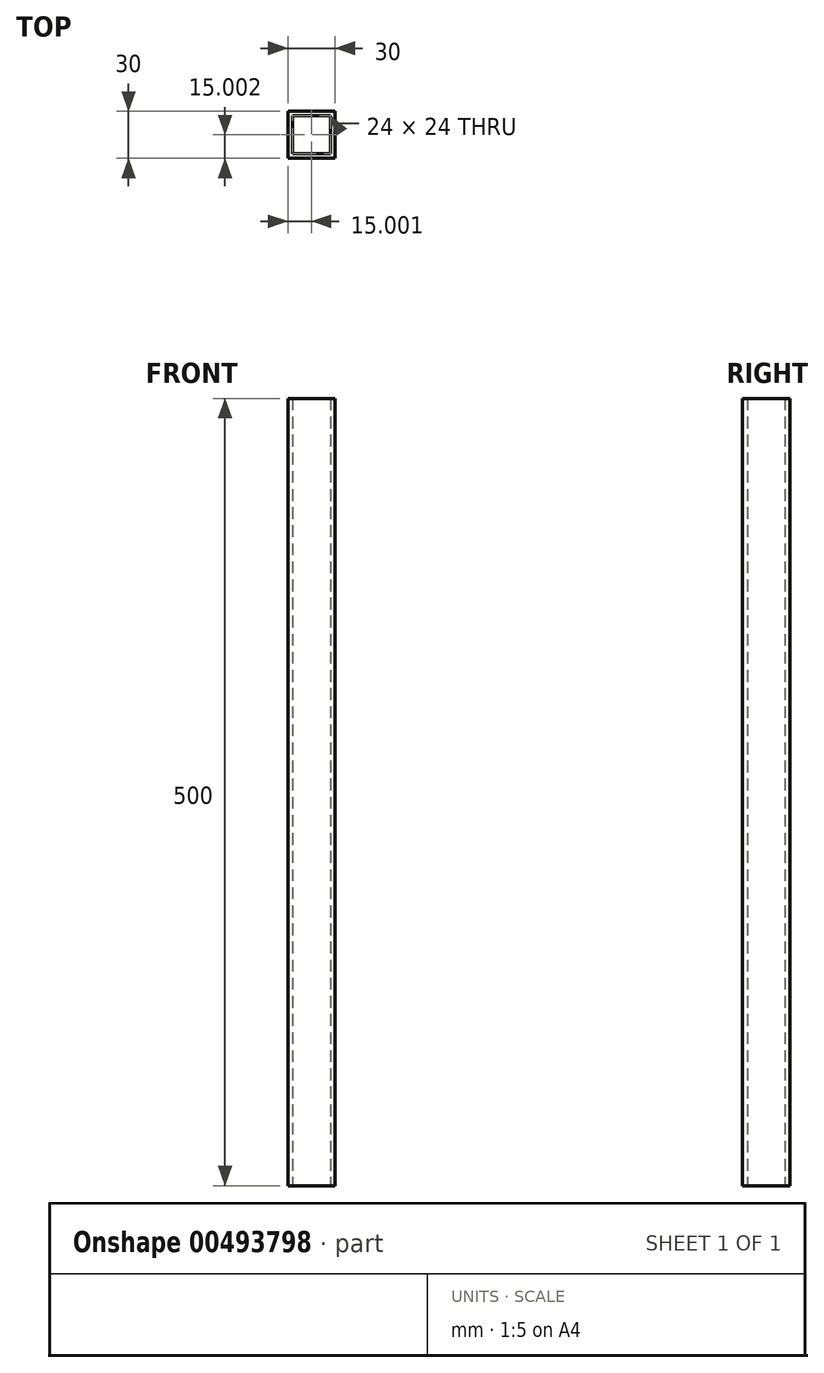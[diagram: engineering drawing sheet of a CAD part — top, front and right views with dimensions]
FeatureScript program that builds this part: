
annotation { "Feature Type Name" : "Feature", "Feature Type Description" : "" }
export const myFeature = defineFeature(function(context is Context, id is Id, definition is map)
    precondition{}
    {
        {
            var Q0;
            Q0=qCreatedBy(makeId("Top.planeOp"),FACE);
            var sketch = newSketch(context, id + "F0", { "sketchPlane" : qUnion([Q0])});
            skLineSegment(sketch, "E0.bottom", {"start": v(-12.6, 13.15) * mm, "end": v(11.4, 13.15) * mm});
            skLineSegment(sketch, "E0.top", {"start": v(-12.6, -10.85) * mm, "end": v(11.4, -10.85) * mm});
            skLineSegment(sketch, "E0.left", {"start": v(-12.6, 13.15) * mm, "end": v(-12.6, -10.85) * mm});
            skLineSegment(sketch, "E0.right", {"start": v(11.4, 13.15) * mm, "end": v(11.4, -10.85) * mm});
            skLineSegment(sketch, "E1.bottom", {"start": v(-15.6, 16.15) * mm, "end": v(14.4, 16.15) * mm});
            skLineSegment(sketch, "E1.top", {"start": v(-15.6, -13.85) * mm, "end": v(14.4, -13.85) * mm});
            skLineSegment(sketch, "E1.left", {"start": v(-15.6, 16.15) * mm, "end": v(-15.6, -13.85) * mm});
            skLineSegment(sketch, "E1.right", {"start": v(14.4, 16.15) * mm, "end": v(14.4, -13.85) * mm});
            skSolve(sketch);
        }
        {
            var Q0;
            Q0=qSketchRegion(id+"F0",true);
            extrude(context, id + "F1", {"entities" : qUnion([Q0]), "depth" : 500 * mm});
        }
    });
